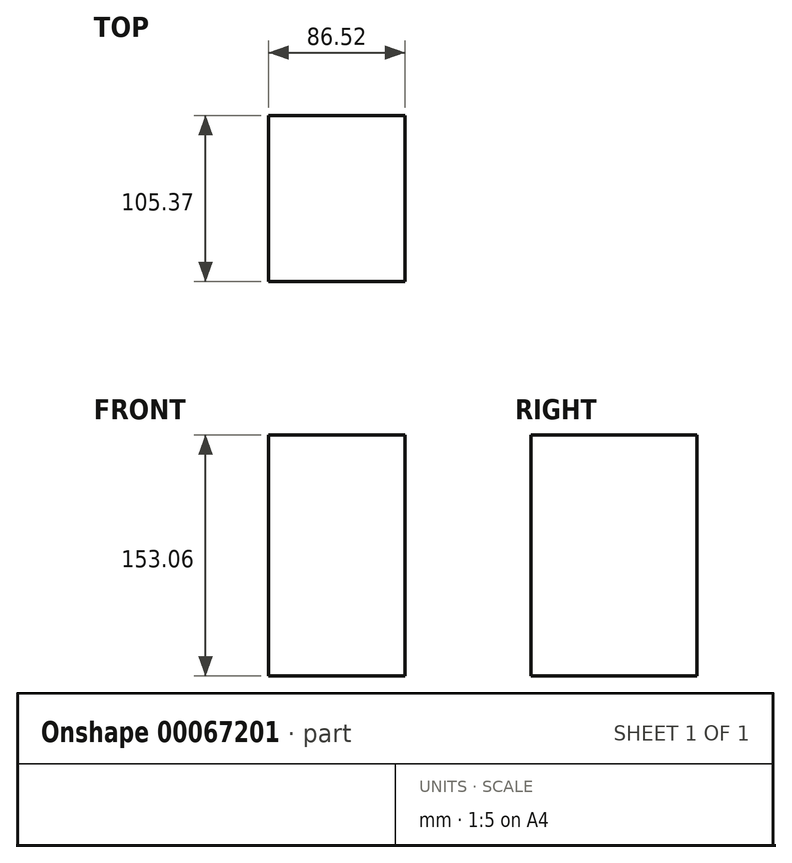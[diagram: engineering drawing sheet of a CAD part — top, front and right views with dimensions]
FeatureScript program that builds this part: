
annotation { "Feature Type Name" : "Feature", "Feature Type Description" : "" }
export const myFeature = defineFeature(function(context is Context, id is Id, definition is map)
    precondition{}
    {
        {
            var Q0;
            Q0=qCreatedBy(makeId("Front.planeOp"),FACE);
            var sketch = newSketch(context, id + "F0", { "sketchPlane" : qUnion([Q0])});
            skLineSegment(sketch, "E0.rect.bottom", {"start": v(43.26, 76.53) * mm, "end": v(-43.26, 76.53) * mm});
            skLineSegment(sketch, "E0.rect.top", {"start": v(43.26, -76.53) * mm, "end": v(-43.26, -76.53) * mm});
            skLineSegment(sketch, "E0.rect.left", {"start": v(43.26, 76.53) * mm, "end": v(43.26, -76.53) * mm});
            skLineSegment(sketch, "E0.rect.right", {"start": v(-43.26, 76.53) * mm, "end": v(-43.26, -76.53) * mm});
            skPoint(sketch, "E0.rect.middle", {"position": v(0, 0) * mm});
            skSolve(sketch);
        }
        {
            var Q0;
            Q0=makeQuery(id+"F0.imprint","IMPRINT",FACE,{"disambiguationData":[TD([[makeQuery(id+"F0.imprint","IMPRINT",EDGE,{"derivedFrom":sQuery(id+"F0.wireOp",EDGE,"E0.rect.bottom")}),1.0]])]});
            extrude(context, id + "F1", {"entities" : qUnion([Q0]), "depth" : 105.37 * mm});
        }
    });
